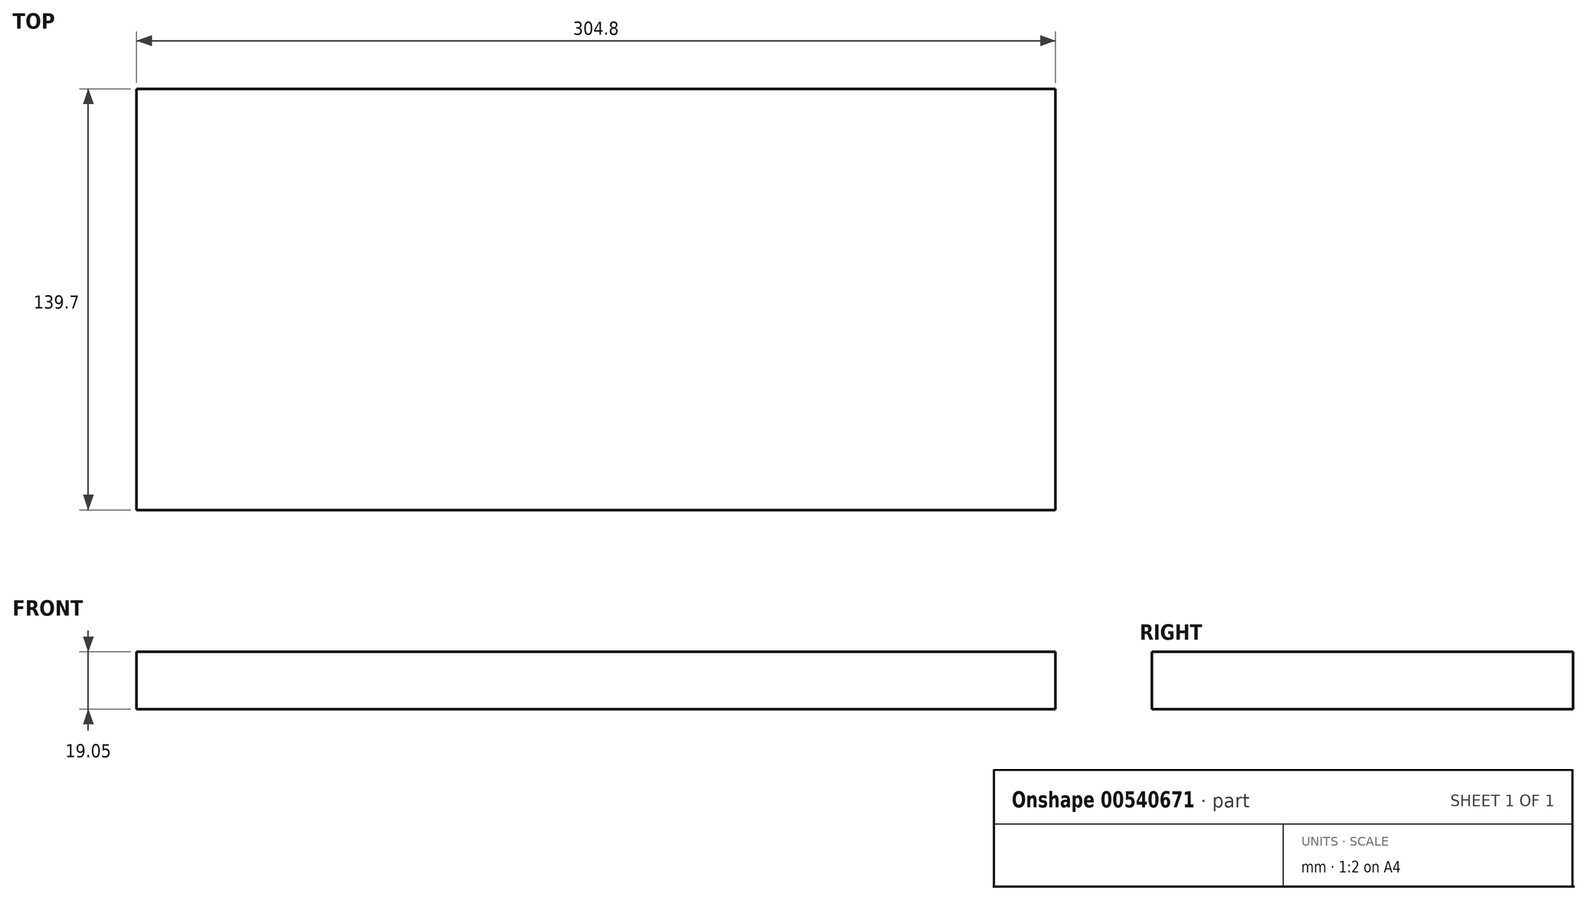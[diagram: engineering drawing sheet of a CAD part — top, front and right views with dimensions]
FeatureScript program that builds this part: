
annotation { "Feature Type Name" : "Feature", "Feature Type Description" : "" }
export const myFeature = defineFeature(function(context is Context, id is Id, definition is map)
    precondition{}
    {
        {
            var Q0;
            Q0=qCreatedBy(makeId("Top.planeOp"),FACE);
            var sketch = newSketch(context, id + "F0", { "sketchPlane" : qUnion([Q0])});
            skLineSegment(sketch, "E0.bottom", {"start": v(-246.52, 71.53) * mm, "end": v(58.28, 71.53) * mm});
            skLineSegment(sketch, "E0.top", {"start": v(-246.52, -68.17) * mm, "end": v(58.28, -68.17) * mm});
            skLineSegment(sketch, "E0.left", {"start": v(-246.52, 71.53) * mm, "end": v(-246.52, -68.17) * mm});
            skLineSegment(sketch, "E0.right", {"start": v(58.28, 71.53) * mm, "end": v(58.28, -68.17) * mm});
            skSolve(sketch);
        }
        {
            var Q0;
            Q0 = qSketchRegion(id + "F0", true);
            extrude(context, id + "F1", {"entities" : qUnion([Q0]), "depth" : 19.05 * mm, "offsetDistance" : 25.4 * mm});
        }
    });
